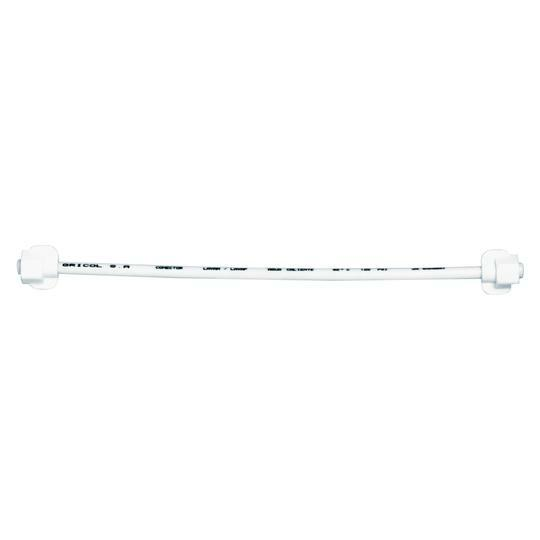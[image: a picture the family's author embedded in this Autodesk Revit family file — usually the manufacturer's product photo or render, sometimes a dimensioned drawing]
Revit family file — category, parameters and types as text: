
# Revit family: BIM_01-1920-00
name_source: partatom
category: Plumbing Fixtures
units: mm (PartAtom-declared; Revit-internal decimal feet)

## family parameters
Classification Number = 23.31.11.00
Cut with Voids When Loaded = No
Enable Cutting in Views = No
Host = Face
Maintain Annotation Orientation = No
Part Type = Normal
Room Calculation Point = No
Round Connector Dimension = Use Diameter
Shared = No

## types (1)
- 01-1920-00
    CW Connection = Yes
    Conexiones = Rosca hembra ½” NPT
    Date Modified = 22/08/2025
    Default Elevation = 0 mm  [stored 0 ft]
    Description = Accesorio
    Diametro = 12.7 mm  [stored 0.0416667 ft]
    Diametro nominal = 5,5 mm
    Empaque-Alto = 40.7 mm  [stored 0.13353 ft]
    Empaque-Ancho = 29.2 mm
    Empaque-Profundidad = 27.3 mm
    Garantia Especifica = 20 AÑOS
    HW Connection = Yes
    Largo = 400 mm  [stored 1.31234 ft]
    Link Ficha Tecnica = https://infotecnica.gricol.com
    Manufacturer = Gricol
    Materiales del producto = ABS, Latón, Acetal, Caucho
    Model = 01-1920-00
    Plastico = Plástico
    Presión Maxima = 125.00 psi
    Presión Mínima = 20.00 psi
    Presión de Estaiildo = 250.00 psi
    Product Name = Conector Lavamanos O Lavaplatos 40 Cm
    Referente Normativo = NTC 5441, ASME A112.18.6 / CSA B125.6
    Resistencia a Corrosión = NTC 1156 Sal Neutral
    Sitio web = https://www.gricol.com
    Temperaturas de trabajo = DE 5° A 71°
    Tipo de Uso = Domestico
    Type Image = CONECTOR LAVAMANOS(PLATOS) H-H ½” X ½”.jpg
    URL = https://www.gricol.com
    Vent Connection = No
    Vida Util = 100000 CICLOS
    Waste Connection = No

note: [stored X ft] marks values corroborated as IEEE doubles in the binary element streams (Revit-internal decimal feet)

## geometry (parser evidence)
native form markers: Blend x8, Sweep x4
no freeform markers — native parametric forms only
